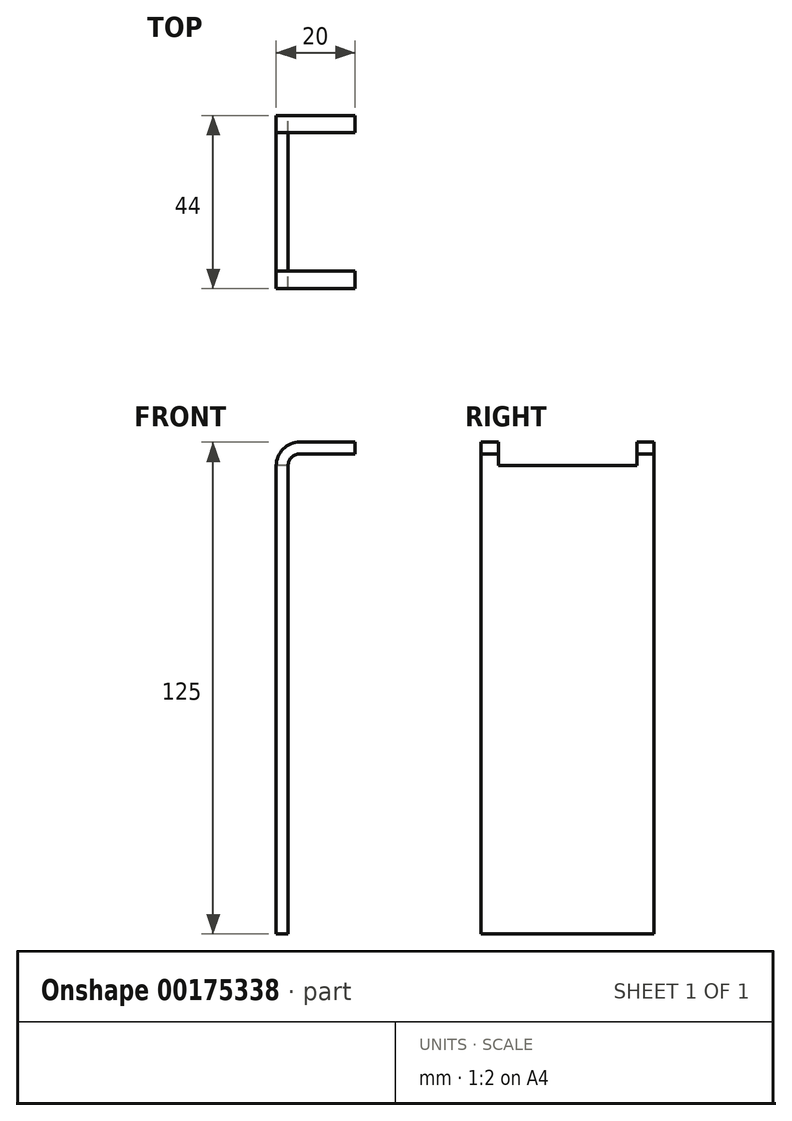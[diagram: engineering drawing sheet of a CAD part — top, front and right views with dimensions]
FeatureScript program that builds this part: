
annotation { "Feature Type Name" : "Feature", "Feature Type Description" : "" }
export const myFeature = defineFeature(function(context is Context, id is Id, definition is map)
    precondition{}
    {
        {
            var Q0;
            Q0=qCreatedBy(makeId("Front.planeOp"),FACE);
            var sketch = newSketch(context, id + "F0", { "sketchPlane" : qUnion([Q0])});
            skLineSegment(sketch, "E0", {"start": v(0, 0) * mm, "end": v(0, 119) * mm});
            skLineSegment(sketch, "E1", {"start": v(3, 122) * mm, "end": v(17, 122) * mm});
            skLineSegment(sketch, "E2.0", {"start": v(3, 125) * mm, "end": v(17, 125) * mm});
            skLineSegment(sketch, "E2.1", {"start": v(-3, 0) * mm, "end": v(-3, 119) * mm});
            skLineSegment(sketch, "E3", {"start": v(17, 125) * mm, "end": v(17, 122) * mm});
            skLineSegment(sketch, "E4", {"start": v(-3, 0) * mm, "end": v(0, 0) * mm});
            skPoint(sketch, "E5.visualSharp", {"position": v(-3, 125) * mm});
            skArc(sketch, "E5.filletArc", {"start": v(3, 125) * mm, "mid": v(-1.24, 123.24) * mm, "end": v(-3, 119) * mm});
            skPoint(sketch, "E6.visualSharp", {"position": v(0, 122) * mm});
            skArc(sketch, "E6.filletArc", {"start": v(3, 122) * mm, "mid": v(0.88, 121.12) * mm, "end": v(0, 119) * mm});
            skSolve(sketch);
        }
        {
            var Q0;
            Q0=makeQuery(id+"F0.imprint","IMPRINT",FACE,{"disambiguationData":[TD([[makeQuery(id+"F0.imprint","IMPRINT",EDGE,{"derivedFrom":sQuery(id+"F0.wireOp",EDGE,"E0")}),1.0]])]});
            extrude(context, id + "F1", {"entities" : qUnion([Q0]), "depth" : 44 * mm});
        }
        {
            var Q0;
            Q0=makeQuery(id+"F1.opExtrude","SWEPT_FACE",FACE,{"disambiguationData":[OSD([sQuery(id+"F0.wireOp",EDGE,"E2.1")])]});
            var sketch = newSketch(context, id + "F2", { "sketchPlane" : qUnion([Q0])});
            skLineSegment(sketch, "E7.bottom", {"start": v(4.4, 119) * mm, "end": v(39.6, 119) * mm});
            skLineSegment(sketch, "E7.top", {"start": v(4.4, 139) * mm, "end": v(39.6, 139) * mm});
            skLineSegment(sketch, "E7.left", {"start": v(4.4, 119) * mm, "end": v(4.4, 139) * mm});
            skLineSegment(sketch, "E7.right", {"start": v(39.6, 119) * mm, "end": v(39.6, 139) * mm});
            skSolve(sketch);
        }
        {
            var Q0;
            Q0=makeQuery(id+"F2.imprint","IMPRINT",FACE,{"disambiguationData":[TD([[makeQuery(id+"F2.imprint","IMPRINT",EDGE,{"derivedFrom":sQuery(id+"F2.wireOp",EDGE,"E7.bottom")}),-1.0]])]});
            extrude(context, id + "F3", {"entities" : qUnion([Q0]), "operationType" : NewBodyOperationType.REMOVE, "endBound" : BoundingType.THROUGH_ALL, "oppositeDirection" : true, "depth" : 25 * mm});
        }
    });
